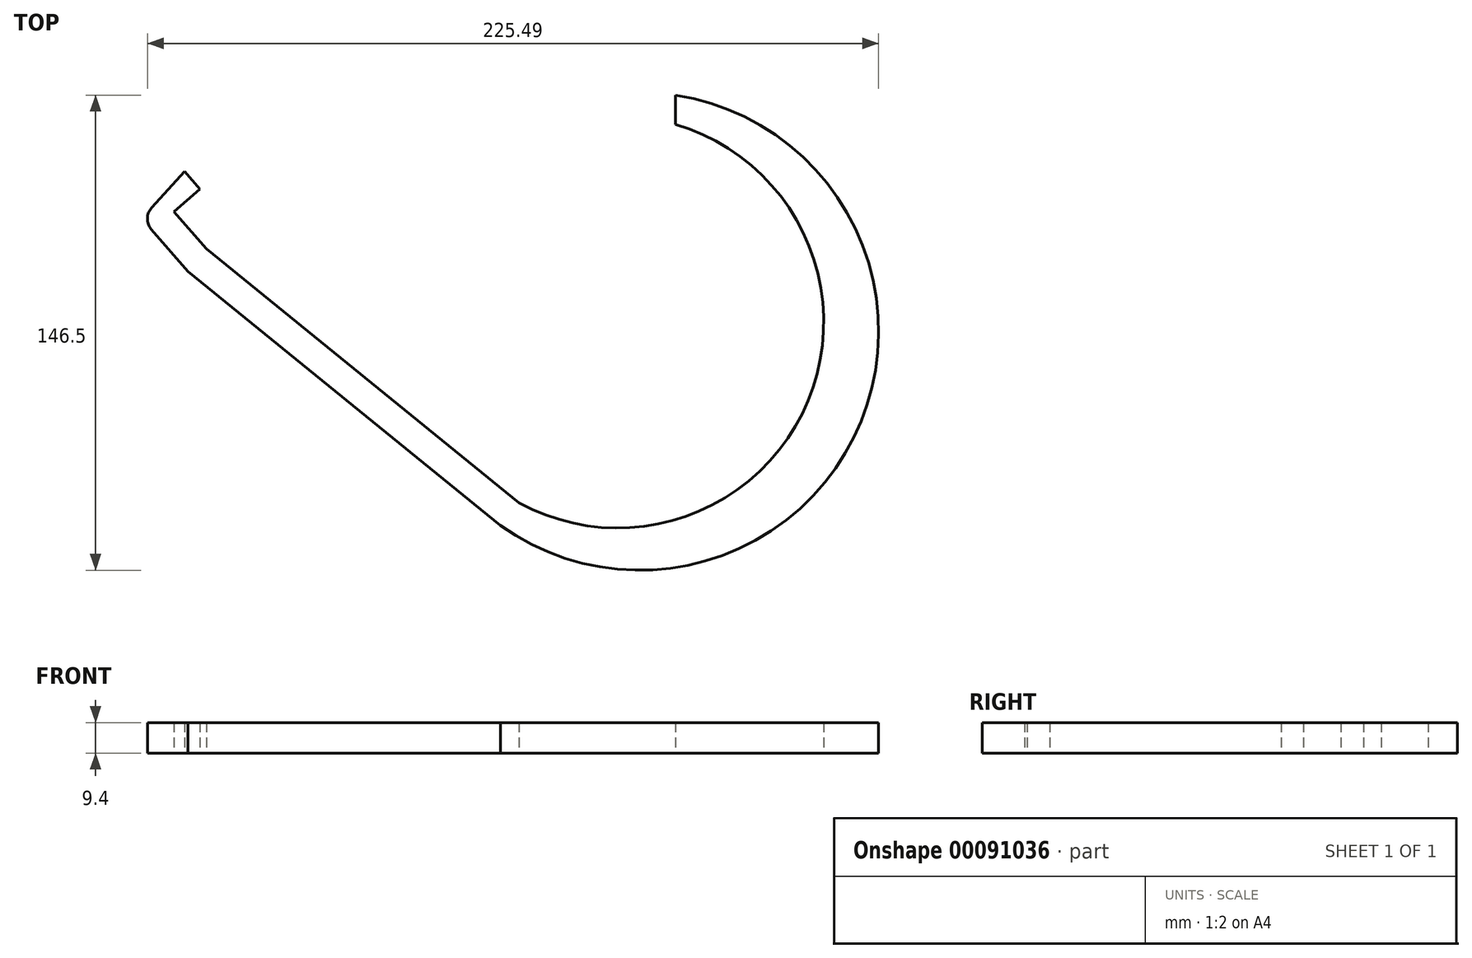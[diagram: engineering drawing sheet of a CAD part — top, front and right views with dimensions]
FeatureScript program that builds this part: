
annotation { "Feature Type Name" : "Feature", "Feature Type Description" : "" }
export const myFeature = defineFeature(function(context is Context, id is Id, definition is map)
    precondition{}
    {
        {
            var Q0;
            Q0=qCreatedBy(makeId("Top.planeOp"),FACE);
            var sketch = newSketch(context, id + "F0", { "sketchPlane" : qUnion([Q0])});
            skArc(sketch, "E0", {"start": v(-156.5, -7) * mm, "mid": v(-45.31, 25.1) * mm, "end": v(-102.54, 125.68) * mm});
            skArc(sketch, "E1", {"start": v(-150.8, 0) * mm, "mid": v(-61.64, 31.42) * mm, "end": v(-102.54, 116.66) * mm});
            skLineSegment(sketch, "E2", {"start": v(-102.54, 125.68) * mm, "end": v(-102.54, 116.66) * mm});
            skLineSegment(sketch, "E3", {"start": v(-150.8, 0) * mm, "end": v(-156.5, -7) * mm});
            skLineSegment(sketch, "E4", {"start": v(-150.8, 0) * mm, "end": v(-247.17, 78.27) * mm});
            skLineSegment(sketch, "E5", {"start": v(-156.5, -7) * mm, "end": v(-252.9, 71.31) * mm});
            skLineSegment(sketch, "E6", {"start": v(-252.9, 71.31) * mm, "end": v(-247.17, 78.27) * mm});
            skLineSegment(sketch, "E7", {"start": v(-267.1, 87.73) * mm, "end": v(-252.9, 71.31) * mm});
            skLineSegment(sketch, "E8", {"start": v(-257.17, 89.76) * mm, "end": v(-247.17, 78.27) * mm});
            skLineSegment(sketch, "E9", {"start": v(-257.17, 89.76) * mm, "end": v(-249.18, 96.72) * mm});
            skLineSegment(sketch, "E10", {"start": v(-249.18, 96.72) * mm, "end": v(-253.95, 102.2) * mm});
            skLineSegment(sketch, "E11", {"start": v(-253.95, 102.2) * mm, "end": v(-267.1, 87.73) * mm});
            skSolve(sketch);
        }
        {
            var Q0;
            Q0=makeQuery(id+"F0.imprint","IMPRINT",FACE,{"disambiguationData":[TD([[makeQuery(id+"F0.imprint","IMPRINT",EDGE,{"derivedFrom":sQuery(id+"F0.wireOp",EDGE,"E3")}),-1.0]])]});
            var Q1;
            Q1=makeQuery(id+"F0.imprint","IMPRINT",FACE,{"disambiguationData":[TD([[makeQuery(id+"F0.imprint","IMPRINT",EDGE,{"derivedFrom":sQuery(id+"F0.wireOp",EDGE,"E0")}),1.0]])]});
            extrude(context, id + "F1", {"entities" : qUnion([Q0, Q1]), "depth" : 9.4 * mm});
        }
        {
            var Q0;
            Q0 = qSketchRegion(id + "F0", true);
            extrude(context, id + "F2", {"entities" : qUnion([Q0]), "operationType" : NewBodyOperationType.ADD, "depth" : 9.4 * mm});
        }
        {
            var Q0;
            Q0=makeQuery(id+"F2.opExtrude","SWEPT_EDGE",EDGE,{"disambiguationData":[OSD([sQuery(id+"F0.wireOp",EDGE,"E7"),sQuery(id+"F0.wireOp",EDGE,"E11")])]});
            fillet(context, id + "F3", {"entities" : qUnion([Q0]), "radius" : 5.08 * mm, "tangentPropagation" : true, "allowEdgeOverflow" : false});
        }
    });
